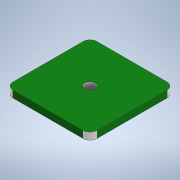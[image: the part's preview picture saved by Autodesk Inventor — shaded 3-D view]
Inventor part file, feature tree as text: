
AUTODESK INVENTOR PART (.ipt)
format: ipt  version: 2022.3 (Build 263350000, 350)  size: 124,928 bytes
history: native  units: mm
features: extrude x2, sketch x2, fillet x1, projected_geometry x1
ambient origin geometry x8: Origin, YZ Plane, XZ Plane, XY Plane, X Axis, Y Axis, Z Axis, Center Point
bodies: Solid1 (feature_tree)
feature tree (6):
  extrude  "Extrusion1"  Depth=24.0mm
  fillet  "Fillet1"  Radius=2.0mm
  extrude  "Extrusion2"  Depth=2.0mm
  sketch  "Sketch1"  dims[d0=24.0mm d1=24.0mm d2=2.0mm d3=0.0mm]
  sketch  "Sketch2"  dims[d4=2.0mm d5=3.0mm d6=2.0mm d7=0.0mm]
  projected_geometry  "Projected Loop1"
